AUTODESK INVENTOR PART (.ipt)
format: ipt  version: 2015 (Build 190159000, 159)  size: 601,088 bytes
history: native  units: in
note: dims shown in document units (in); Inventor stores cm internally (conversion verified against a paired STEP export)
features: projected_geometry x18, other x17, sketch x16, extrude x8, loft x8, plane x6, mirror x2
ambient origin geometry x8: Origin, YZ Plane, XZ Plane, XY Plane, X Axis, Y Axis, Z Axis, Center Point
bodies: Solid1 (feature_tree)
feature tree (75):
  other  "BatteryBox.ipt"
  extrude  "Extrusion1"  Depth=0.25in
  extrude  "Extrusion2"  Depth=0.25in TaperAngle=0.0deg
  extrude  "Extrusion3"  TaperAngle=0.0deg  [1 undecoded]
  sketch  "Sketch4"  dims[d10=0.0in d11=90.0deg d12=0.0in d13=90.0deg]
  plane  "Work Plane1"
  sketch  "Sketch5"  dims[d14=0.0in d15=90.0deg d16=0.0in d17=90.0deg]
  other  "Work Point2"
  sketch  "Sketch7"  dims[d18=0.0in d19=90.0deg d20=0.0in d21=90.0deg]
  plane  "Work Plane2"
  sketch  "Sketch8"  dims[d22=0.0in d23=90.0deg d24=0.0in d25=90.0deg]
  other  "Work Point3"
  sketch  "Sketch9"  dims[d26=0.0in d27=90.0deg d28=0.0in d29=90.0deg]
  plane  "Work Plane3"
  sketch  "Sketch10"  dims[d30=0.0in d31=90.0deg d32=0.0in d33=90.0deg]
  loft  "Loft1"
  loft  "Loft2"
  loft  "Loft3"
  loft  "Loft4"
  other  "Work Point4"
  other  "Work Point5"
  sketch  "Sketch11"  dims[d34=0.0in d35=90.0deg d36=0.0in d37=90.0deg]
  plane  "Work Plane4"
  sketch  "Sketch12"  dims[d38=0.0in d39=90.0deg d40=0.25in d41=0.0in]
  loft  "Loft5"
  loft  "Loft6"
  plane  "Work Plane5"
  mirror  "Mirror1"
  loft  "Loft7"
  loft  "Loft8"
  extrude  "Extrusion4"  [1 undecoded]
  extrude  "Extrusion5"  Depth=0.25in
  plane  "Work Plane6"
  extrude  "Extrusion6"  Depth=0.25in
  mirror  "Mirror2"
  extrude  "Extrusion7"  Depth=0.25in
  extrude  "Extrusion8"  Depth=0.25in
  other  "TaggingFeature1"
  sketch  "Sketch1"  dims[d0=0.3937in d1=0.25in]
  sketch  "Sketch2"  dims[d2=1.0in d3=0.0in d4=0.25in d5=0.0in]
  sketch  "Sketch3"  dims[d6=0.25in d7=0.0in d8=0.0in d9=90.0deg]
  other  "Edges1"
  other  "Edges2"
  other  "Edges3"
  other  "Work Axis1"
  other  "Work Point6"
  other  "Edges4"
  sketch  "Sketch14"  dims[d42=0.25in d43=0.0in d44=-0.25in]
  other  "Edges5"
  other  "Edges6"
  other  "Edges7"
  sketch  "Sketch15"  dims[d45=0.25in d46=0.0in d47=0.375in]
  projected_geometry  "Projected Loop1"
  sketch  "Sketch16"  dims[d48=0.25in d49=0.0in d50=0.25in]
  sketch  "Sketch17"  dims[d51=0.25in d52=1.5in]
  sketch  "Sketch18"  dims[d53=1.25in d54=0.25in d55=0.438in d56=0.625in d57=0.25in d58=0.0in]
  other  "Solid1::BatteryBox.ipt"
  other  "Srf1"
  projected_geometry  "Project Cut Edges1"
  projected_geometry  "Project Cut Edges2"
  projected_geometry  "Project Cut Edges3"
  projected_geometry  "Project Cut Edges4"
  projected_geometry  "Project Cut Edges6"
  projected_geometry  "Project Cut Edges7"
  projected_geometry  "Project Cut Edges8"
  projected_geometry  "Project Cut Edges9"
  projected_geometry  "Project Cut Edges10"
  projected_geometry  "Project Cut Edges11"
  projected_geometry  "Project Cut Edges12"
  projected_geometry  "Project Cut Edges13"
  projected_geometry  "Project Cut Edges14"
  projected_geometry  "Project Cut Edges15"
  projected_geometry  "Project Cut Edges16"
  projected_geometry  "Project Cut Edges17"
  projected_geometry  "Project Cut Edges18"
note: 2 required parameter values undecoded (feature->parameter linkage not recoverable at this tier; creation-order binding heuristic only, values carry confidence <= 0.55)
